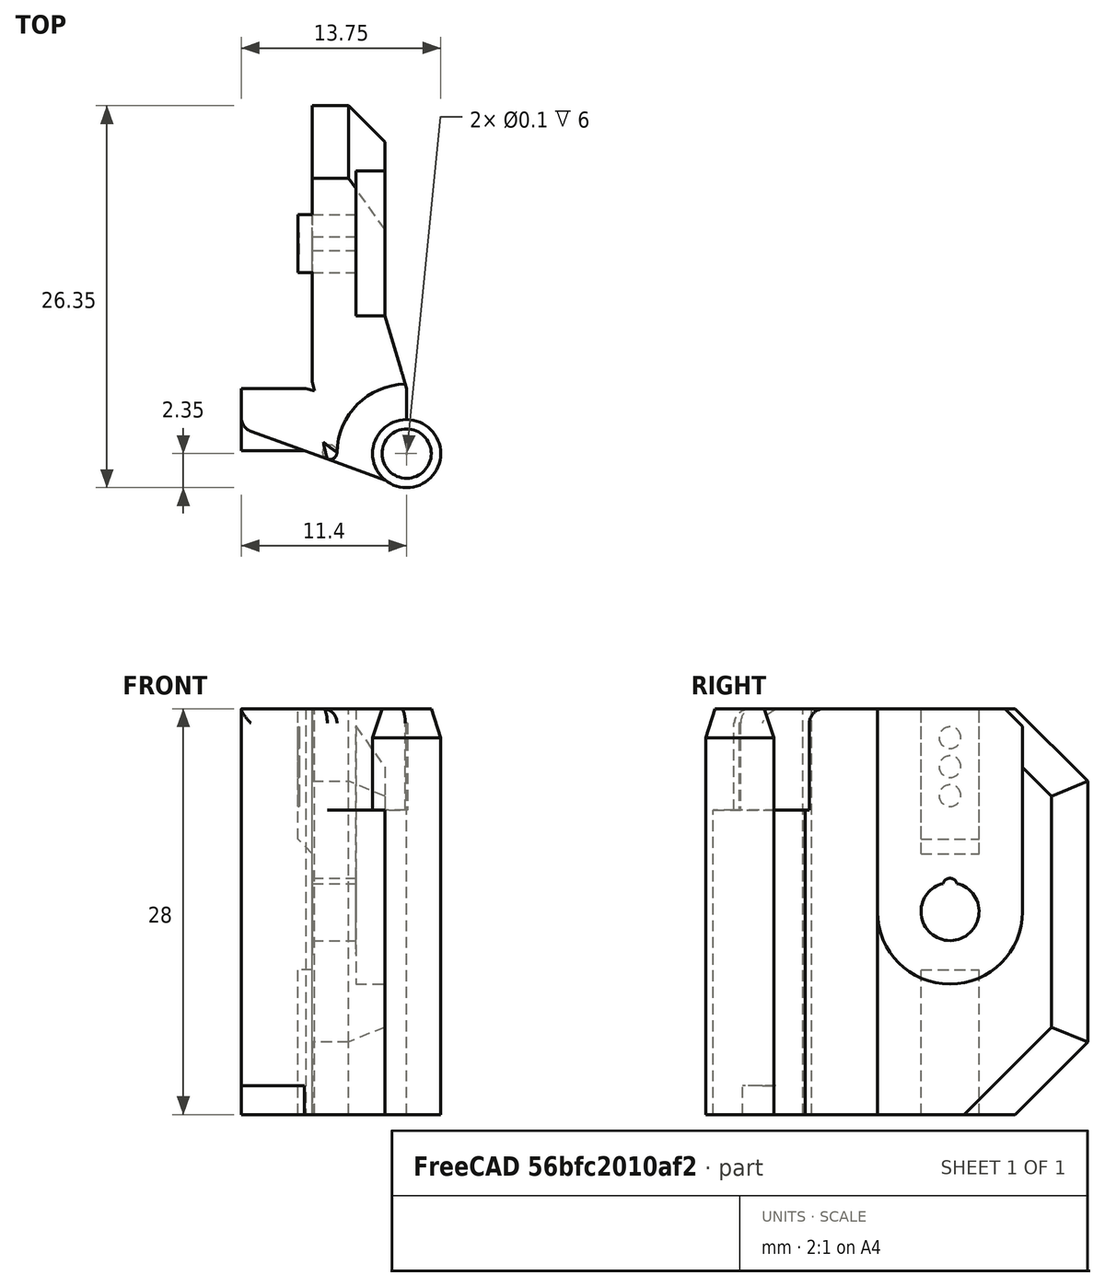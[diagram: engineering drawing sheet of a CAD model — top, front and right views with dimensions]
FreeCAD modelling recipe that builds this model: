
FCSTD DOCUMENT  (FreeCAD 0.18R14555 (Git shallow))
Label: hingle-top
License: All rights reserved
LicenseURL: http://en.wikipedia.org/wiki/All_rights_reserved
objects: Part::Feature×4, Part::Cut×2, Part::Box×1, Part::Chamfer×1, App::Part×1, Part::MultiFuse×1
note: 9 computed .brp shape members not serialized (recipe doc carries the construction recipe); baked Part::Feature solids carry a one-line shape summary decoded from their .brp

FEATURE [Part::Feature] Part__Feature008  label="m5-to-m4-bolt-hole001"
  Placement = pos=(-3.5,14.5,14) rot=(0,0,-1;1.5708rad)
  shape: bbox 3 x 6 x 6 mm, 5 faces (baked)
FEATURE [Part::Box] Box006  label="Cube006"
  AttacherType = Attacher::AttachEngine3D
  Height = 9
  Length = 2
  Placement = pos=(-22.5,0,0) rot=(0,0,1;0rad)
  Width = 11
FEATURE [Part::Chamfer] Chamfer
  Base = -> Box006
  Edges = 1 edges r=1: [Edge6]
  Placement = pos=(14,8,10) rot=(0,0,1;0rad)
FEATURE [Part::Feature] Part__Feature003  label="rambo_hinge_upper"
  Placement = pos=(0,0,0) rot=(0,1,0;3.14159rad)
  shape: bbox 14.09 x 26.35 x 28 mm, 52 faces (baked)
FEATURE [App::Part] rambo_hinge_upper_v1  label="rambo_hinge_upper v1"
  Group = -> [Part__Feature003]
  Origin = -> Origin003
FEATURE [Part::Feature] Part__Feature  label="t-slot-align"
  Placement = pos=(-6.5,19.73,-1.4e-15) rot=(-0.57735,0.57735,-0.57735;4.18879rad)
  shape: bbox 5 x 10.45 x 60 mm, 10 faces (baked)
FEATURE [Part::Cut] Cut
  Base = -> Part__Feature003
  Tool = -> Part__Feature
FEATURE [Part::Cut] Cut001
  Base = -> Cut
  Tool = -> Chamfer
FEATURE [Part::MultiFuse] Fusion
  Shapes = -> [Cut001,Part__Feature008]
FEATURE [Part::Feature] Fusion001
  shape: bbox 14.09 x 26.35 x 28 mm, 52 faces (baked)
